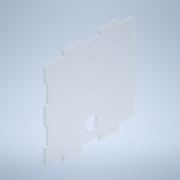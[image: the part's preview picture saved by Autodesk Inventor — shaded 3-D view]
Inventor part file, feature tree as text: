
AUTODESK INVENTOR PART (.ipt)
format: ipt  version: 2020 (Build 240168000, 168)  size: 194,560 bytes
history: native  units: mm
features: sketch x10, hole x9, extrude x1
ambient origin geometry x8: Origin, YZ Plane, XZ Plane, XY Plane, X Axis, Y Axis, Z Axis, Center Point
bodies: Solid1 (feature_tree)
feature tree (20):
  extrude  "Extrusion1"  Depth=3.0mm
  hole  "Hole2"  [1 undecoded]
  hole  "Hole3"  [1 undecoded]
  hole  "Hole4"  [1 undecoded]
  hole  "Hole5"  [1 undecoded]
  hole  "Hole6"  [1 undecoded]
  hole  "Hole7"  [1 undecoded]
  hole  "Hole8"  [1 undecoded]
  hole  "Hole9"  [1 undecoded]
  hole  "Hole10"  [1 undecoded]
  sketch  "Sketch1"  dims[d4=3.0mm d5=0.0mm d22=3.0mm]
  sketch  "Sketch3"  dims[d23=3.0mm d24=6.0mm d25=4.0mm d26=2.0mm d27=90.0deg d28=8.0mm d29=20.594885mm d30=3.0mm]
  sketch  "Sketch4"  dims[d31=3.0mm d32=6.0mm d33=4.0mm d34=2.0mm d35=90.0deg d36=8.0mm d37=20.594885mm d38=3.0mm]
  sketch  "Sketch5"  dims[d39=3.0mm d40=6.0mm d41=4.0mm d42=2.0mm d43=90.0deg d44=8.0mm d45=20.594885mm d46=3.0mm]
  sketch  "Sketch6"  dims[d47=15.0mm d48=6.0mm d49=4.0mm d50=2.0mm d51=90.0deg d52=8.0mm d53=20.594885mm d54=3.0mm]
  sketch  "Sketch7"  dims[d55=3.0mm d56=6.0mm d57=4.0mm d58=2.0mm d59=90.0deg d60=8.0mm d61=20.594885mm d62=3.0mm]
  sketch  "Sketch8"  dims[d63=3.0mm d64=6.0mm d65=4.0mm d66=2.0mm d67=90.0deg d68=8.0mm d69=20.594885mm d70=3.0mm]
  sketch  "Sketch9"  dims[d71=3.0mm d72=6.0mm d73=4.0mm d74=2.0mm d75=90.0deg d76=8.0mm d77=20.594885mm d78=3.0mm]
  sketch  "Sketch10"  dims[d79=3.0mm d80=6.0mm d81=4.0mm d82=2.0mm d83=90.0deg d84=8.0mm d85=20.594885mm d86=3.0mm]
  sketch  "Sketch11"  dims[d87=3.0mm d88=6.0mm d89=4.0mm d90=2.0mm d91=90.0deg d92=8.0mm d93=20.594885mm d94=1.0mm d95=10.0mm d96=1.0mm d97=1.0mm d98=10.0mm d99=10.0mm]
note: 9 required parameter values undecoded (feature->parameter linkage not recoverable at this tier; creation-order binding heuristic only, values carry confidence <= 0.55)
